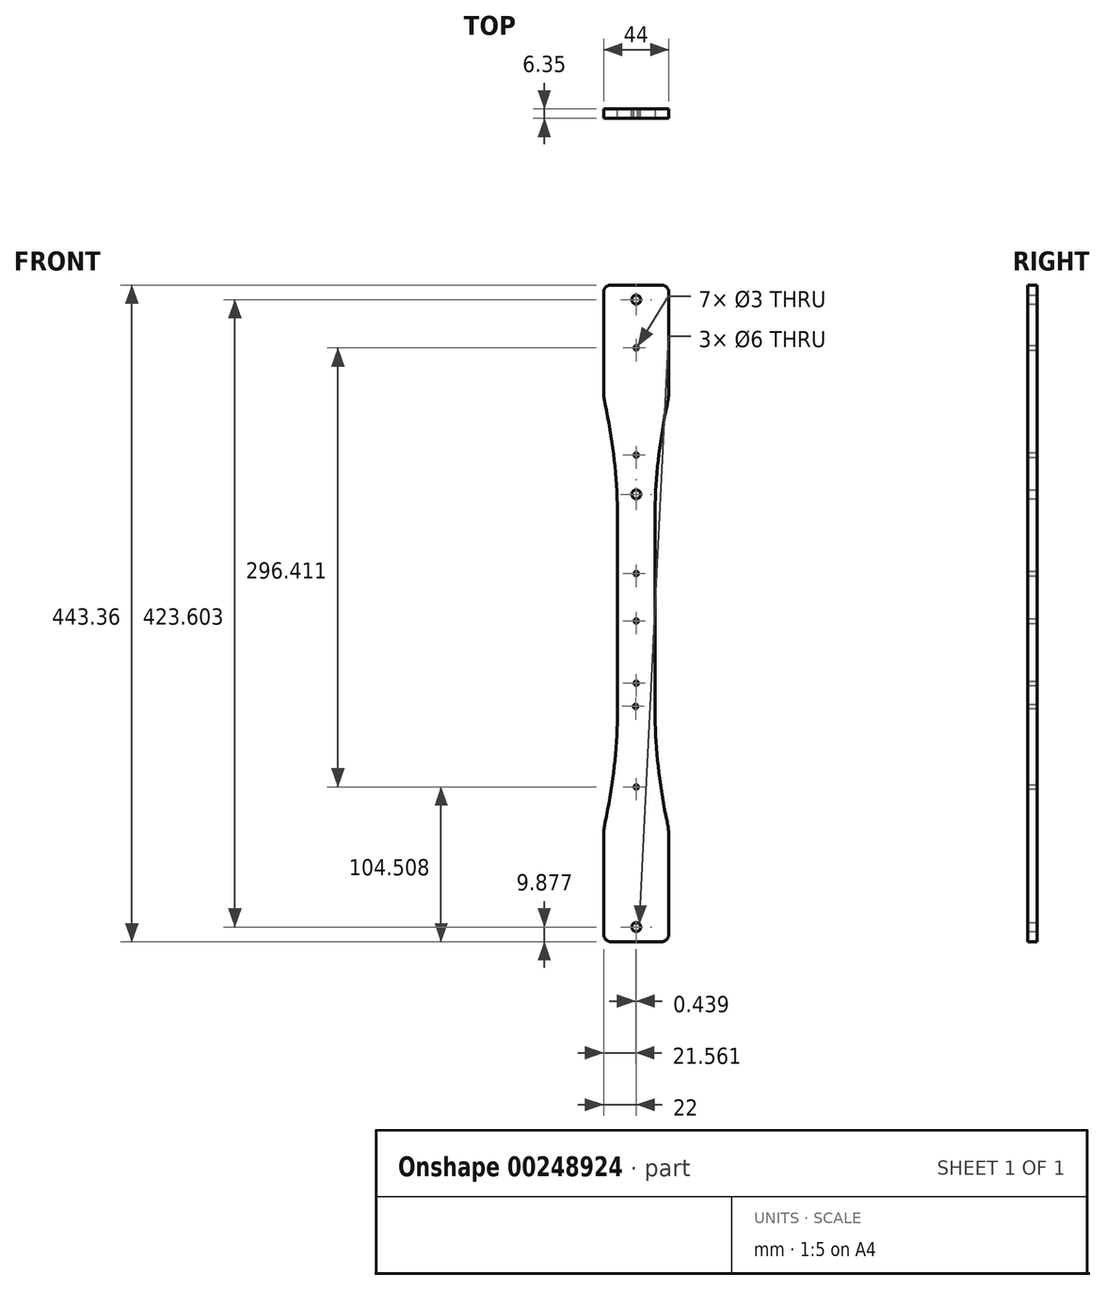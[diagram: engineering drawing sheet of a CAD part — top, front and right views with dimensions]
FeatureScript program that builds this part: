
annotation { "Feature Type Name" : "Feature", "Feature Type Description" : "" }
export const myFeature = defineFeature(function(context is Context, id is Id, definition is map)
    precondition{}
    {
        {
            var Q0;
            Q0=qCreatedBy(makeId("Front.planeOp"),FACE);
            var sketch = newSketch(context, id + "F0", { "sketchPlane" : qUnion([Q0])});
            skCircle(sketch, "E0", {"center": v(0, -85.45) * mm, "radius": 1.5 * mm});
            skCircle(sketch, "E1", {"center": v(-0.44, -31.05) * mm, "radius": 1.5 * mm});
            skCircle(sketch, "E2", {"center": v(0, 26.55) * mm, "radius": 1.5 * mm});
            skLineSegment(sketch, "E3.top", {"start": v(-4.69, -189.96) * mm, "end": v(4.69, -189.96) * mm});
            skLineSegment(sketch, "E3.left", {"start": v(-12.7, 245.38) * mm, "end": v(-12.7, 177.2) * mm});
            skLineSegment(sketch, "E3.right", {"start": v(12.7, 245.38) * mm, "end": v(12.7, 177.2) * mm});
            skPoint(sketch, "E4.visualSharp", {"position": v(12.7, 263.22) * mm});
            skPoint(sketch, "E5.visualSharp", {"position": v(12.7, -189.96) * mm});
            skArc(sketch, "E5.filletArc", {"start": v(4.69, -189.96) * mm, "mid": v(10.35, -187.61) * mm, "end": v(12.7, -181.95) * mm});
            skPoint(sketch, "E6.visualSharp", {"position": v(-12.7, -189.96) * mm});
            skArc(sketch, "E6.filletArc", {"start": v(-12.7, -181.95) * mm, "mid": v(-10.35, -187.61) * mm, "end": v(-4.69, -189.96) * mm});
            skCircle(sketch, "E7", {"center": v(0, 58.56) * mm, "radius": 1.5 * mm});
            skLineSegment(sketch, "E8", {"start": v(0, 26.55) * mm, "end": v(0, 99.81) * mm, "construction": true});
            skLineSegment(sketch, "E9", {"start": v(0, 99.81) * mm, "end": v(0, -85.45) * mm, "construction": true});
            skLineSegment(sketch, "E10", {"start": v(0, -85.45) * mm, "end": v(0, -201.73) * mm, "construction": true});
            skCircle(sketch, "E11", {"center": v(0, 243.52) * mm, "radius": 3 * mm});
            skCircle(sketch, "E12", {"center": v(0, -15.45) * mm, "radius": 1.5 * mm});
            skLineSegment(sketch, "E13", {"start": v(0, 58.56) * mm, "end": v(0, 424.12) * mm});
            skCircle(sketch, "E14", {"center": v(0, 210.96) * mm, "radius": 1.5 * mm});
            skCircle(sketch, "E15", {"center": v(0, 138.56) * mm, "radius": 1.5 * mm});
            skLineSegment(sketch, "E16", {"start": v(12.7, 31.72) * mm, "end": v(-12.7, 31.72) * mm, "construction": true});
            skArc(sketch, "E17.MirrorCS", {"start": v(-12.7, 245.38) * mm, "mid": v(-12.15, 248.3) * mm, "end": v(-10.58, 250.82) * mm});
            skArc(sketch, "E18.MirrorCS", {"start": v(10.58, 250.82) * mm, "mid": v(12.15, 248.3) * mm, "end": v(12.7, 245.38) * mm});
            skLineSegment(sketch, "E19.MirrorCS", {"start": v(-4.69, 253.4) * mm, "end": v(4.69, 253.4) * mm});
            skPoint(sketch, "E20.end.orphan", {"position": v(-12.7, 257.02) * mm});
            skPoint(sketch, "E21.orphan", {"position": v(-12.7, 249.87) * mm});
            skPoint(sketch, "E22.orphan", {"position": v(-7.5, 253.51) * mm});
            skPoint(sketch, "E23.end.orphan", {"position": v(12.7, 257.02) * mm});
            skPoint(sketch, "E23.start.orphan", {"position": v(12.7, 258.21) * mm});
            skPoint(sketch, "E24.start.orphan", {"position": v(7.5, 253.51) * mm});
            skCircle(sketch, "E25", {"center": v(0, -180.08) * mm, "radius": 3 * mm});
            skCircle(sketch, "E26", {"center": v(0, 112.09) * mm, "radius": 3 * mm});
            skLineSegment(sketch, "E27", {"start": v(12.7, 162.23) * mm, "end": v(-12.7, 162.23) * mm});
            skLineSegment(sketch, "E28", {"start": v(12.7, 177.2) * mm, "end": v(-12.7, 177.2) * mm});
            skLineSegment(sketch, "E29.trimOffspring", {"start": v(-12.7, 162.23) * mm, "end": v(-12.7, -95.1) * mm});
            skLineSegment(sketch, "E30.trimOffspring", {"start": v(12.7, 162.23) * mm, "end": v(12.7, -95.1) * mm});
            skLineSegment(sketch, "E31", {"start": v(12.7, -113.76) * mm, "end": v(-12.7, -113.76) * mm});
            skLineSegment(sketch, "E32", {"start": v(12.7, -95.1) * mm, "end": v(-12.7, -95.1) * mm});
            skLineSegment(sketch, "E33.trimOffspring", {"start": v(-12.7, -113.76) * mm, "end": v(-12.7, -181.95) * mm});
            skLineSegment(sketch, "E34.trimOffspring", {"start": v(12.7, -113.76) * mm, "end": v(12.7, -181.95) * mm});
            skLineSegment(sketch, "E35", {"start": v(-22, 177.54) * mm, "end": v(-22, 236.3) * mm});
            skLineSegment(sketch, "E36.MirrorCS", {"start": v(22, 177.54) * mm, "end": v(22, 236.3) * mm});
            skArc(sketch, "E37", {"start": v(-12.7, 104.8) * mm, "mid": v(-15.58, 141.4) * mm, "end": v(-22, 177.54) * mm});
            skArc(sketch, "E38.MirrorCS", {"start": v(12.7, 104.8) * mm, "mid": v(15.58, 141.4) * mm, "end": v(22, 177.54) * mm});
            skPoint(sketch, "E39.orphan", {"position": v(-4.69, 253.4) * mm});
            skPoint(sketch, "E40.orphan", {"position": v(-22, 240.87) * mm});
            skPoint(sketch, "E41.orphan", {"position": v(4.69, 253.4) * mm});
            skPoint(sketch, "E42.orphan", {"position": v(22, 240.87) * mm});
            skLineSegment(sketch, "E43", {"start": v(0, 253.4) * mm, "end": v(-22, 253.4) * mm});
            skLineSegment(sketch, "E44", {"start": v(-22, 225.43) * mm, "end": v(-22, 253.4) * mm});
            skPoint(sketch, "E45.orphan", {"position": v(-33.54, 253.4) * mm});
            skLineSegment(sketch, "E46.MirrorCS", {"start": v(22, 225.43) * mm, "end": v(22, 253.4) * mm});
            skLineSegment(sketch, "E47.MirrorCS", {"start": v(0, 253.4) * mm, "end": v(22, 253.4) * mm});
            skArc(sketch, "E48.MirrorCS", {"start": v(12.7, -41.36) * mm, "mid": v(15.58, -77.96) * mm, "end": v(22, -114.1) * mm});
            skLineSegment(sketch, "E49.MirrorCS", {"start": v(22, -114.1) * mm, "end": v(22, -172.87) * mm});
            skArc(sketch, "E50.MirrorCS", {"start": v(-12.7, -41.36) * mm, "mid": v(-15.58, -77.96) * mm, "end": v(-22, -114.1) * mm});
            skLineSegment(sketch, "E51.MirrorCS", {"start": v(-22, -114.1) * mm, "end": v(-22, -172.87) * mm});
            skLineSegment(sketch, "E52.MirrorCS", {"start": v(0, -189.96) * mm, "end": v(-22, -189.96) * mm});
            skLineSegment(sketch, "E53.MirrorCS", {"start": v(0, -189.96) * mm, "end": v(22, -189.96) * mm});
            skLineSegment(sketch, "E54.MirrorCS", {"start": v(22, -162) * mm, "end": v(22, -189.96) * mm});
            skLineSegment(sketch, "E55.MirrorCS", {"start": v(-22, -162) * mm, "end": v(-22, -189.96) * mm});
            skSolve(sketch);
        }
        {
            var Q0;
            Q0=makeQuery(id+"F0.imprint","IMPRINT",FACE,{"disambiguationData":[TD([[makeQuery(id+"F0.imprint","IMPRINT",EDGE,{"derivedFrom":sQuery(id+"F0.wireOp",EDGE,"E0")}),-1.0]])]});
            var Q1;
            {var subQ8=sQuery(id+"F0.wireOp",EDGE,"E3.left");Q1=makeQuery(id+"F0.imprint","IMPRINT",FACE,{"disambiguationData":[TD([[makeQuery(id+"F0.imprint","IMPRINT",EDGE,{"derivedFrom":subQ8}),-1.0]])]});}
            var Q2;
            {var subQ10=sQuery(id+"F0.wireOp",EDGE,"E3.right");Q2=makeQuery(id+"F0.imprint","IMPRINT",FACE,{"disambiguationData":[TD([[makeQuery(id+"F0.imprint","IMPRINT",EDGE,{"derivedFrom":subQ10}),1.0]])]});}
            var Q3;
            {var subQ8=sQuery(id+"F0.wireOp",EDGE,"E3.right");Q3=makeQuery(id+"F0.imprint","IMPRINT",FACE,{"disambiguationData":[TD([[makeQuery(id+"F0.imprint","IMPRINT",EDGE,{"derivedFrom":subQ8}),-1.0]])]});}
            var Q4;
            {var subQ8=sQuery(id+"F0.wireOp",EDGE,"E3.left");Q4=makeQuery(id+"F0.imprint","IMPRINT",FACE,{"disambiguationData":[TD([[makeQuery(id+"F0.imprint","IMPRINT",EDGE,{"derivedFrom":subQ8}),1.0]])]});}
            var Q5;
            {var subQ0=sQuery(id+"F0.wireOp",EDGE,"ywFLEBLb-G5Qe-hJVo-9jNG-EmXgII5EXrAz");Q5=makeQuery(id+"F0.imprint","IMPRINT",FACE,{"disambiguationData":[TD([[makeQuery(id+"F0.imprint","IMPRINT",EDGE,{"derivedFrom":subQ0}),-1.0]])]});}
            var Q6;
            {var subQ17=sQuery(id+"F0.wireOp",EDGE,"E35");Q6=makeQuery(id+"F0.imprint","IMPRINT",FACE,{"disambiguationData":[TD([[makeQuery(id+"F0.imprint","IMPRINT",EDGE,{"derivedFrom":subQ17}),-1.0]])]});}
            var Q7;
            {var subQ4=sQuery(id+"F0.wireOp",EDGE,"E36.MirrorCS");Q7=makeQuery(id+"F0.imprint","IMPRINT",FACE,{"disambiguationData":[TD([[makeQuery(id+"F0.imprint","IMPRINT",EDGE,{"derivedFrom":subQ4}),1.0]])]});}
            var Q8;
            {var subQ2=sQuery(id+"F0.wireOp",EDGE,"E5.filletArc");Q8=makeQuery(id+"F0.imprint","IMPRINT",FACE,{"disambiguationData":[TD([[makeQuery(id+"F0.imprint","IMPRINT",EDGE,{"derivedFrom":subQ2}),-1.0]])]});}
            var Q9;
            {var subQ1=sQuery(id+"F0.wireOp",EDGE,"E5.filletArc");Q9=makeQuery(id+"F0.imprint","IMPRINT",FACE,{"disambiguationData":[TD([[makeQuery(id+"F0.imprint","IMPRINT",EDGE,{"derivedFrom":subQ1}),1.0]])]});}
            extrude(context, id + "F1", {"entities" : qUnion([Q0, Q1, Q2, Q3, Q4, Q5, Q6, Q7, Q8, Q9]), "depth" : 6.35 * mm});
        }
        {
            var Q0;
            Q0=makeQuery(id+"F1.opExtrude","SWEPT_EDGE",EDGE,{"disambiguationData":[OSD([sQuery(id+"F0.wireOp",EDGE,"E43"),sQuery(id+"F0.wireOp",EDGE,"E44")])]});
            var Q1;
            Q1=makeQuery(id+"F1.opExtrude","SWEPT_EDGE",EDGE,{"disambiguationData":[OSD([sQuery(id+"F0.wireOp",EDGE,"E46.MirrorCS"),sQuery(id+"F0.wireOp",EDGE,"E47.MirrorCS")])]});
            var Q2;
            Q2=makeQuery(id+"F1.opExtrude","SWEPT_EDGE",EDGE,{"disambiguationData":[OSD([sQuery(id+"F0.wireOp",EDGE,"E53.MirrorCS"),sQuery(id+"F0.wireOp",EDGE,"E54.MirrorCS")])]});
            var Q3;
            Q3=makeQuery(id+"F1.opExtrude","SWEPT_EDGE",EDGE,{"disambiguationData":[OSD([sQuery(id+"F0.wireOp",EDGE,"E52.MirrorCS"),sQuery(id+"F0.wireOp",EDGE,"E55.MirrorCS")])]});
            fillet(context, id + "F2", {"entities" : qUnion([Q0, Q1, Q2, Q3]), "radius" : 5.08 * mm, "tangentPropagation" : true, "allowEdgeOverflow" : false});
        }
        {
            var Q0;
            Q0=makeQuery(id+"F1.opExtrude","SWEPT_EDGE",EDGE,{"disambiguationData":[OSD([sQuery(id+"F0.wireOp",EDGE,"E50.MirrorCS"),sQuery(id+"F0.wireOp",EDGE,"E51.MirrorCS")])]});
            var Q1;
            Q1=makeQuery(id+"F1.opExtrude","SWEPT_EDGE",EDGE,{"disambiguationData":[OSD([sQuery(id+"F0.wireOp",EDGE,"E48.MirrorCS"),sQuery(id+"F0.wireOp",EDGE,"E49.MirrorCS")])]});
            var Q2;
            Q2=makeQuery(id+"F1.opExtrude","SWEPT_EDGE",EDGE,{"disambiguationData":[OSD([sQuery(id+"F0.wireOp",EDGE,"E36.MirrorCS"),sQuery(id+"F0.wireOp",EDGE,"E38.MirrorCS")])]});
            var Q3;
            Q3=makeQuery(id+"F1.opExtrude","SWEPT_EDGE",EDGE,{"disambiguationData":[OSD([sQuery(id+"F0.wireOp",EDGE,"E35"),sQuery(id+"F0.wireOp",EDGE,"E37")])]});
            var Q4;
            Q4=makeQuery(id+"F1.opExtrude","SWEPT_EDGE",EDGE,{"disambiguationData":[OSD([sQuery(id+"F0.wireOp",EDGE,"E29.trimOffspring"),sQuery(id+"F0.wireOp",EDGE,"E37")])]});
            var Q5;
            Q5=makeQuery(id+"F1.opExtrude","SWEPT_EDGE",EDGE,{"disambiguationData":[OSD([sQuery(id+"F0.wireOp",EDGE,"E30.trimOffspring"),sQuery(id+"F0.wireOp",EDGE,"E38.MirrorCS")])]});
            var Q6;
            Q6=makeQuery(id+"F1.opExtrude","SWEPT_EDGE",EDGE,{"disambiguationData":[OSD([sQuery(id+"F0.wireOp",EDGE,"E30.trimOffspring"),sQuery(id+"F0.wireOp",EDGE,"E48.MirrorCS")])]});
            var Q7;
            Q7=makeQuery(id+"F1.opExtrude","SWEPT_EDGE",EDGE,{"disambiguationData":[OSD([sQuery(id+"F0.wireOp",EDGE,"E29.trimOffspring"),sQuery(id+"F0.wireOp",EDGE,"E50.MirrorCS")])]});
            fillet(context, id + "F3", {"entities" : qUnion([Q0, Q1, Q2, Q3, Q4, Q5, Q6, Q7]), "radius" : 50.8 * mm, "tangentPropagation" : true, "allowEdgeOverflow" : false});
        }
    });
